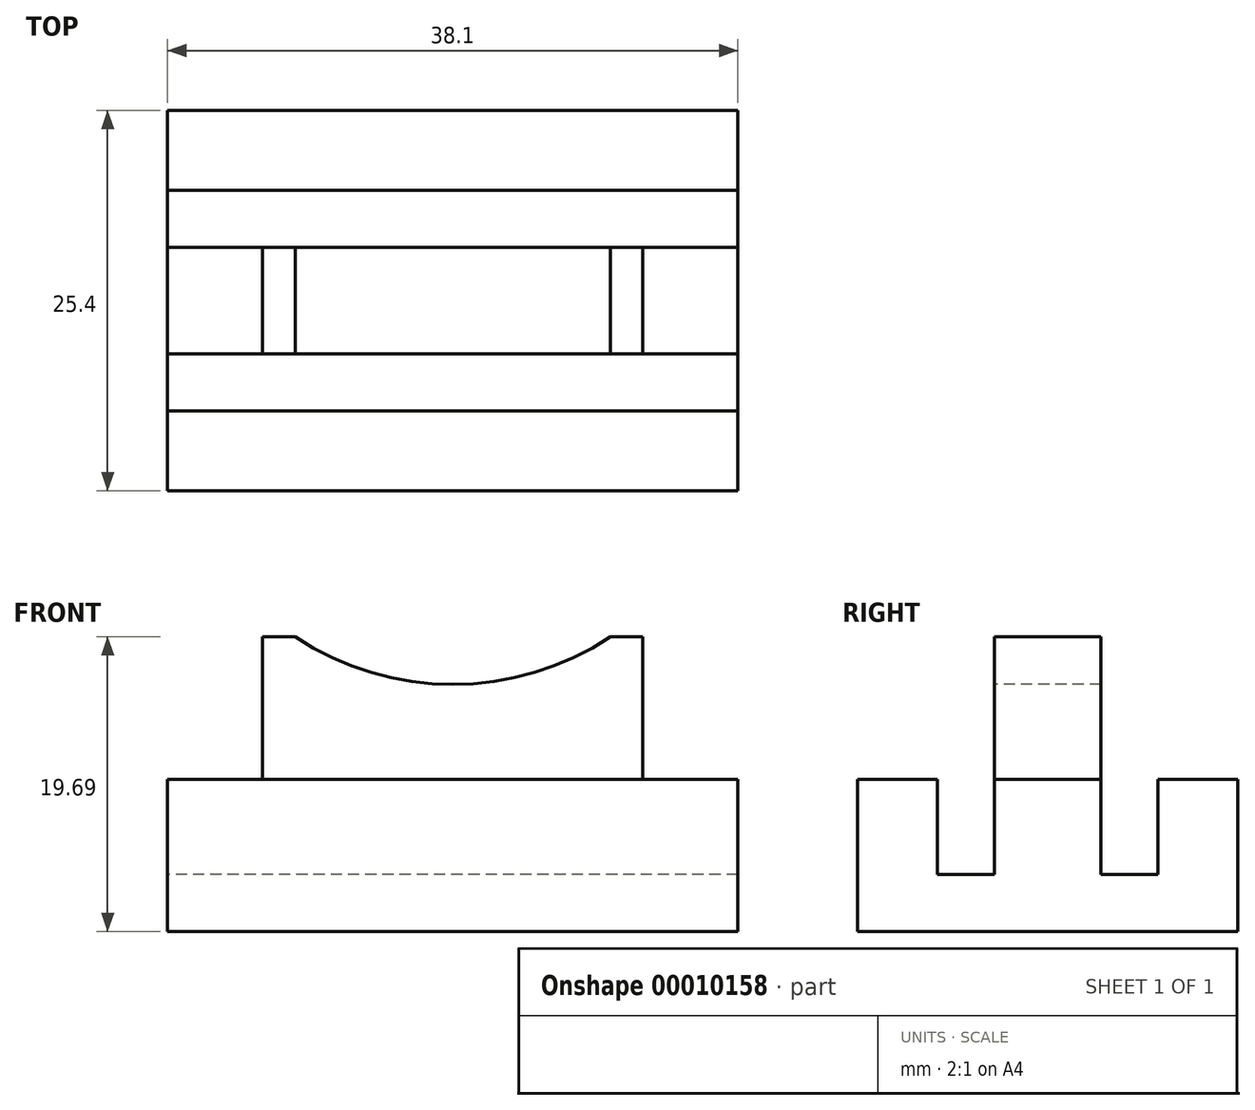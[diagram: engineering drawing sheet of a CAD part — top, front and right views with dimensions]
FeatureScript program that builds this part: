
annotation { "Feature Type Name" : "Feature", "Feature Type Description" : "" }
export const myFeature = defineFeature(function(context is Context, id is Id, definition is map)
    precondition{}
    {
        {
            var Q0;
            Q0=qCreatedBy(makeId("Top.planeOp"),FACE);
            var sketch = newSketch(context, id + "F0", { "sketchPlane" : qUnion([Q0])});
            skLineSegment(sketch, "E0.rect.bottom", {"start": v(19.05, 12.7) * mm, "end": v(-19.05, 12.7) * mm});
            skLineSegment(sketch, "E0.rect.top", {"start": v(19.05, -12.7) * mm, "end": v(-19.05, -12.7) * mm});
            skLineSegment(sketch, "E0.rect.left", {"start": v(19.05, 12.7) * mm, "end": v(19.05, -12.7) * mm});
            skLineSegment(sketch, "E0.rect.right", {"start": v(-19.05, 12.7) * mm, "end": v(-19.05, -12.7) * mm});
            skPoint(sketch, "E0.rect.middle", {"position": v(0, 0) * mm});
            skSolve(sketch);
        }
        {
            var Q0;
            Q0=makeQuery(id+"F0.imprint","IMPRINT",FACE,{"disambiguationData":[TD([[makeQuery(id+"F0.imprint","IMPRINT",EDGE,{"derivedFrom":sQuery(id+"F0.wireOp",EDGE,"E0.rect.bottom")}),1.0]])]});
            extrude(context, id + "F1", {"entities" : qUnion([Q0]), "depth" : 10.16 * mm});
        }
        {
            var Q0;
            Q0=makeQuery(id+"F1.opExtrude","CAP_FACE",FACE,{"disambiguationData":[OSD([sQuery(id+"F0.wireOp",EDGE,"E0.rect.bottom"),sQuery(id+"F0.wireOp",EDGE,"E0.rect.top"),sQuery(id+"F0.wireOp",EDGE,"E0.rect.left"),sQuery(id+"F0.wireOp",EDGE,"E0.rect.right")])],"isStart":false});
            var sketch = newSketch(context, id + "F2", { "sketchPlane" : qUnion([Q0])});
            skLineSegment(sketch, "E1.rect.bottom", {"start": v(12.7, 3.56) * mm, "end": v(-12.7, 3.56) * mm});
            skLineSegment(sketch, "E1.rect.top", {"start": v(12.7, -3.56) * mm, "end": v(-12.7, -3.56) * mm});
            skLineSegment(sketch, "E1.rect.left", {"start": v(12.7, 3.56) * mm, "end": v(12.7, -3.56) * mm});
            skLineSegment(sketch, "E1.rect.right", {"start": v(-12.7, 3.56) * mm, "end": v(-12.7, -3.56) * mm});
            skPoint(sketch, "E1.rect.middle", {"position": v(0, 0) * mm});
            skSolve(sketch);
        }
        {
            var Q0;
            Q0 = qSketchRegion(id + "F2", true);
            extrude(context, id + "F3", {"entities" : qUnion([Q0]), "operationType" : NewBodyOperationType.ADD, "depth" : 9.52 * mm});
        }
        {
            var Q0;
            Q0=makeQuery(id+"F3.opExtrude","SWEPT_FACE",FACE,{"disambiguationData":[OSD([sQuery(id+"F2.wireOp",EDGE,"E1.rect.top")])]});
            var sketch = newSketch(context, id + "F4", { "sketchPlane" : qUnion([Q0])});
            skCircle(sketch, "E2", {"center": v(0, 35.56) * mm, "radius": 19.05 * mm});
            skSolve(sketch);
        }
        {
            var Q0;
            {var subQ0=makeQuery(id+"F3.opExtrude","CAP_EDGE",EDGE,{"disambiguationData":[OSD([sQuery(id+"F2.wireOp",EDGE,"E1.rect.top")])],"isStart":false});var subQ1=sQuery(id+"F4.wireOp",EDGE,"E2");var subQ3=makeQuery(id+"F4.imprint","INTERSECT",VERTEX,{"disambiguationData":[OD(0.0)],"derivedFrom":[subQ0,subQ1]});Q0=makeQuery(id+"F4.imprint","IMPRINT",FACE,{"disambiguationData":[TD([[makeQuery(id+"F4.imprint","IMPRINT",EDGE,{"disambiguationData":[TD([[subQ3,1.0]])],"derivedFrom":subQ1}),1.0]])]});}
            extrude(context, id + "F5", {"entities" : qUnion([Q0]), "operationType" : NewBodyOperationType.REMOVE, "endBound" : BoundingType.UP_TO_NEXT, "oppositeDirection" : true, "depth" : 25.4 * mm});
        }
        {
            var Q0;
            Q0=makeQuery(id+"F1.opExtrude","CAP_FACE",FACE,{"disambiguationData":[OSD([sQuery(id+"F0.wireOp",EDGE,"E0.rect.bottom"),sQuery(id+"F0.wireOp",EDGE,"E0.rect.top"),sQuery(id+"F0.wireOp",EDGE,"E0.rect.left"),sQuery(id+"F0.wireOp",EDGE,"E0.rect.right")])],"isStart":false});
            var sketch = newSketch(context, id + "F6", { "sketchPlane" : qUnion([Q0])});
            skLineSegment(sketch, "E3.rect.bottom", {"start": v(19.05, 3.56) * mm, "end": v(-19.05, 3.56) * mm});
            skLineSegment(sketch, "E3.rect.top", {"start": v(19.05, 7.37) * mm, "end": v(-19.05, 7.37) * mm});
            skLineSegment(sketch, "E3.rect.left", {"start": v(19.05, 3.56) * mm, "end": v(19.05, 7.37) * mm});
            skLineSegment(sketch, "E3.rect.right", {"start": v(-19.05, 3.56) * mm, "end": v(-19.05, 7.37) * mm});
            skPoint(sketch, "E3.rect.middle", {"position": v(0, 5.46) * mm});
            skLineSegment(sketch, "E4.rect.bottom", {"start": v(19.05, -3.56) * mm, "end": v(-19.05, -3.56) * mm});
            skLineSegment(sketch, "E4.rect.top", {"start": v(19.05, -7.37) * mm, "end": v(-19.05, -7.37) * mm});
            skLineSegment(sketch, "E4.rect.left", {"start": v(19.05, -3.56) * mm, "end": v(19.05, -7.37) * mm});
            skLineSegment(sketch, "E4.rect.right", {"start": v(-19.05, -3.56) * mm, "end": v(-19.05, -7.37) * mm});
            skPoint(sketch, "E4.rect.middle", {"position": v(0, -5.46) * mm});
            skSolve(sketch);
        }
        {
            var Q0;
            Q0 = qSketchRegion(id + "F6", true);
            extrude(context, id + "F7", {"entities" : qUnion([Q0]), "operationType" : NewBodyOperationType.REMOVE, "oppositeDirection" : true, "depth" : 6.35 * mm});
        }
    });
